# Revit family: Sanitary_Bath-Spas_DURAVIT-AG_Cape-Cod-Bathtub-1650x780-mm-700459
name_source: partatom
category: Plumbing Fixtures
revit_build: Autodesk Revit 2018 (Build: 20180329_1100(x64)
units: mm (PartAtom-declared; Revit-internal decimal feet)

## family parameters
Always vertical = No
Cut with Voids When Loaded = No
OmniClass Number = 23.31.15.00
OmniClass Title = Bathtubs
Part Type = Normal
Room Calculation Point = No
Round Connector Dimension = Use Diameter
Shared = No
Work Plane-Based = Yes

## types (1)
- Cape Cod Bathtub 1650x780 mm - 700459
    BIMobject category = Bath & Spas
    Connector Description = Water outlet
    Default Elevation = 1219.2 mm  [stored 4 ft]
    Description = Duravit Cape Cod Bathtub, 1650x780 mm White Matt, Freestanding, Seamless panel, Polymer cast - DuraSolid A, Oval, Number of backrests: 2, Overflow, Incl. cable-driven waste and overflow, Special waste and overflow - 700459000000000
    Design country = Germany
    Details material = Duravit - Metal - 10 - Chrome
    ETIM classification = EC011609 | Bath
    Edition number = 1
    IFC Classification = Sanitary Terminal
    Installation instructions = http://pro.duravit.com
    Main material = Duravit - Plastic - 00 - White Alpin
    Manufacturer = Duravit
    Manufacturer name = DURAVIT AG
    Masterformat 2014 Code = 22 41 19
    Masterformat 2014 Description = Residential Bathtubs
    Material main = Polymer
    Model = Cape Cod Bathtub 1650x780 mm - 700459
    OmniClass Code = 23-31 15 00
    OmniClass Description = Bathtubs
    Outlet Diameter = 50 mm
    Product Guid = 38727fff-c4f9-42e6-9376-208da7ba2120
    Product SKU = Cape-Cod-Bathtub-1650x780-mm-700459
    Product certification = http://pro.duravit.com
    Product data url = https://bimobject.com
    Product family = Cape Code
    Product group = Bathtub
    Product name = Cape Cod Bathtub 1650x780 mm - 700459
    Product url = http://pro.duravit.com
    QR code = https://bimobject.com
    Technical description = http://pro.duravit.com
    UNSPSC Code = 30181501
    URL = https://www.duravit.com
    Uniclass 2015 Code = Pr_40_20_06_08
    Uniclass 2015 Name = Baths
    Uniformat II Code = D2010
    Uniformat II Description = Plumbing Fixtures
    Weight Net (Kg) = 95
    Youtube clip = http://pro.duravit.com

note: [stored X ft] marks values corroborated as IEEE doubles in the binary element streams (Revit-internal decimal feet)

## geometry (parser evidence)
native form markers: Sweep x4
no freeform markers — native parametric forms only
